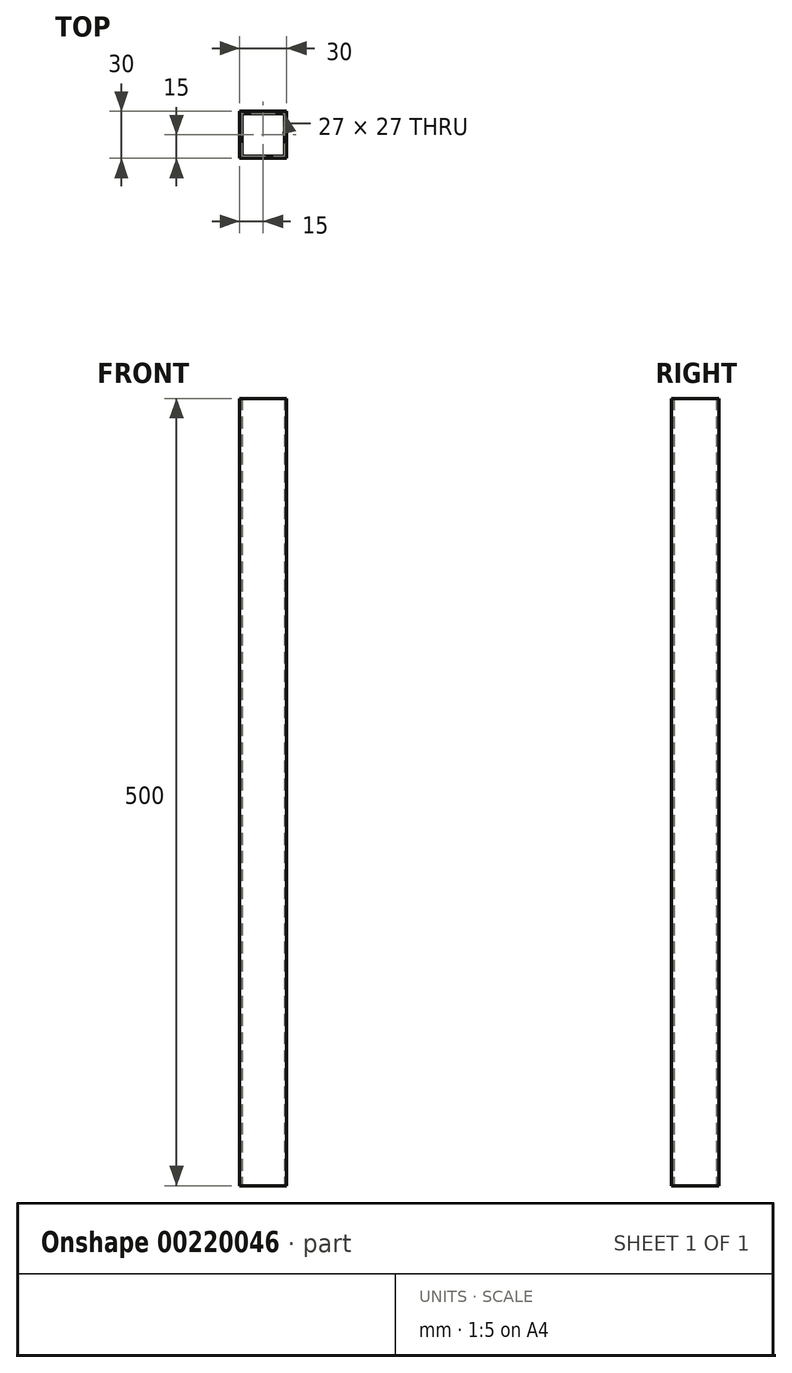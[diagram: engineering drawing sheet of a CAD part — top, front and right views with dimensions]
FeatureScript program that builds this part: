
annotation { "Feature Type Name" : "Feature", "Feature Type Description" : "" }
export const myFeature = defineFeature(function(context is Context, id is Id, definition is map)
    precondition{}
    {
        {
            var Q0;
            Q0=qCreatedBy(makeId("Top.planeOp"),FACE);
            var sketch = newSketch(context, id + "F0", { "sketchPlane" : qUnion([Q0])});
            skLineSegment(sketch, "E0.bottom", {"start": v(0, 0) * mm, "end": v(30, 0) * mm});
            skLineSegment(sketch, "E0.top", {"start": v(0, -30) * mm, "end": v(30, -30) * mm});
            skLineSegment(sketch, "E0.left", {"start": v(0, 0) * mm, "end": v(0, -30) * mm});
            skLineSegment(sketch, "E0.right", {"start": v(30, 0) * mm, "end": v(30, -30) * mm});
            skLineSegment(sketch, "E1.bottom", {"start": v(1.5, -1.5) * mm, "end": v(28.5, -1.5) * mm});
            skLineSegment(sketch, "E1.top", {"start": v(1.5, -28.5) * mm, "end": v(28.5, -28.5) * mm});
            skLineSegment(sketch, "E1.left", {"start": v(1.5, -1.5) * mm, "end": v(1.5, -28.5) * mm});
            skLineSegment(sketch, "E1.right", {"start": v(28.5, -1.5) * mm, "end": v(28.5, -28.5) * mm});
            skSolve(sketch);
        }
        {
            var Q0;
            Q0=makeQuery(id+"F0.imprint","IMPRINT",FACE,{"disambiguationData":[TD([[makeQuery(id+"F0.imprint","IMPRINT",EDGE,{"derivedFrom":sQuery(id+"F0.wireOp",EDGE,"E0.bottom")}),-1.0]])]});
            extrude(context, id + "F1", {"entities" : qUnion([Q0]), "depth" : 500 * mm});
        }
    });
